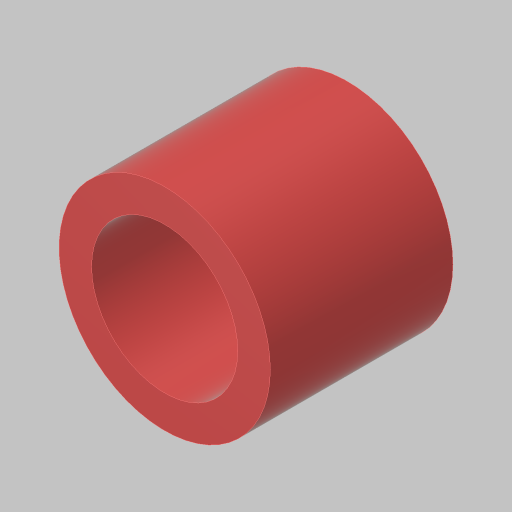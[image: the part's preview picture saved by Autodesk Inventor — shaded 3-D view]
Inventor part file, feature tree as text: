
AUTODESK INVENTOR PART (.ipt)
format: ipt  version: 2023.5 (Build 275446000, 446)  size: 114,176 bytes
history: native  units: in
note: dims shown in document units (in); Inventor stores cm internally (conversion verified against a paired STEP export)
features: extrude x1, sketch x1
ambient origin geometry x8: Origin, YZ Plane, XZ Plane, XY Plane, X Axis, Y Axis, Z Axis, Center Point
bodies: Solid1 (feature_tree)
feature tree (2):
  extrude  "Extrusion1"  Depth=0.7in
  sketch  "Sketch1"  dims[d0=0.56in d1=0.125in d2=0.7in d3=0.0in]
